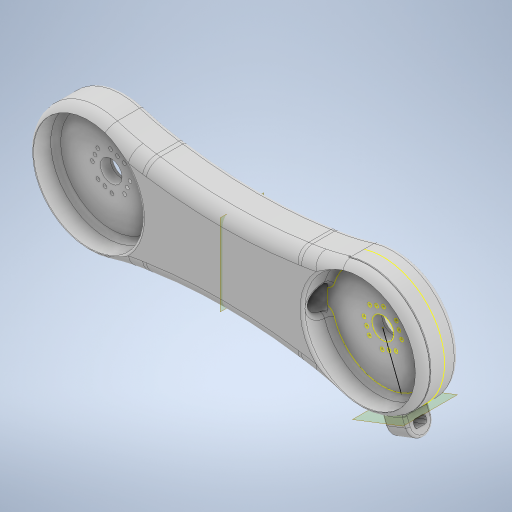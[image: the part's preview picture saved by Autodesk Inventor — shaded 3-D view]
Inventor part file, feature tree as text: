
AUTODESK INVENTOR PART (.ipt)
format: ipt  version: 2024 (Build 280153000, 153)  size: 2,071,552 bytes
history: native  units: mm
features: fillet x13, extrude x9, other x4, plane x3, projected_geometry x3, mirror x2, reference x1, sketch x1
ambient origin geometry x8: Origin, YZ Plane, XZ Plane, XY Plane, X Axis, Y Axis, Z Axis, Center Point
bodies: Solid1 (feature_tree)
feature tree (36):
  plane  "Work Plane1"
  extrude  "Extrusion1"  Depth=1.0mm TaperAngle=0.0deg
  extrude  "Extrusion2"  Depth=1.0mm
  extrude  "Extrusion3"  Depth=1.0mm TaperAngle=0.0deg
  extrude  "Extrusion4"  Depth=1.0mm
  extrude  "Extrusion5"  Depth=1.0mm
  fillet  "Fillet1"  Radius=15.0mm
  fillet  "Fillet2"  Radius=10.0mm
  fillet  "Fillet3"  Radius=20.0mm
  plane  "Work Plane3"
  mirror  "Mirror2"
  mirror  "Mirror3"
  fillet  "Fillet4"  Radius=20.0mm
  fillet  "Fillet5"  Radius=2.837941mm
  extrude  "Extrusion6"  Depth=1.0mm
  fillet  "Fillet6"  Radius=6.0mm
  fillet  "Fillet7"  Radius=10.0mm
  fillet  "Fillet10"  Radius=8.0mm
  fillet  "Fillet11"  Radius=10.0mm
  plane  "Work Plane5"
  extrude  "Extrusion11"  Depth=1.0mm
  extrude  "Extrusion12"  Depth=1.0mm
  extrude  "Extrusion13"  Depth=1.0mm
  fillet  "Fillet14"  [1 undecoded]
  fillet  "Fillet15"  Radius=200.0mm
  fillet  "Fillet16"  Radius=100.0mm
  fillet  "Fillet17"  Radius=70.0mm
  reference  "Reference1"
  projected_geometry  "Projected Loop1"
  sketch  "Sketch3"  dims[d0=50.0mm d1=6.0mm d2=0.0mm d3=45.0mm d4=10.0mm d5=0.0mm d6=55.0mm d7=15.0mm d8=15.0mm d9=10.0mm d10=0.0mm d12=20.0mm d13=20.0mm d14=2.837941mm d15=12.817996mm d16=6.0mm d17=0.0mm d18=10.0mm d19=8.0mm d20=10.0mm d21=0.0mm d22=2.0mm d23=2.0mm d24=1.0mm d25=0.0mm d26=200.0mm d27=100.0mm d28=70.0mm d29=0.0mm d30=1.0mm d31=1.0mm d53=5.0mm d54=2.0mm d57=10.0mm d58=10.0mm d59=2.5mm d60=0.0mm d61=9.0mm d62=0.0mm d63=5.0mm d64=3.0mm d65=5.0mm d66=5.0mm d67=0.0mm d68=0.0mm d69=1.0mm d70=1.0mm d71=5.0mm d72=1.0mm d73=0.0mm d74=0.0mm d75=0.0mm d76=0.0mm]
  projected_geometry  "Projected Loop2"
  projected_geometry  "Projected Loop3"
  other  "<userpath> windows\Documents\Inventor\Robotska_roka\Assembly4.iam"
  other  "Assembly4.iam"
  other  "Servo Motor MG996R  With Attachments:4"
  other  "attachmentCircular_1"
note: 1 required parameter value undecoded (feature->parameter linkage not recoverable at this tier; creation-order binding heuristic only, values carry confidence <= 0.55)
